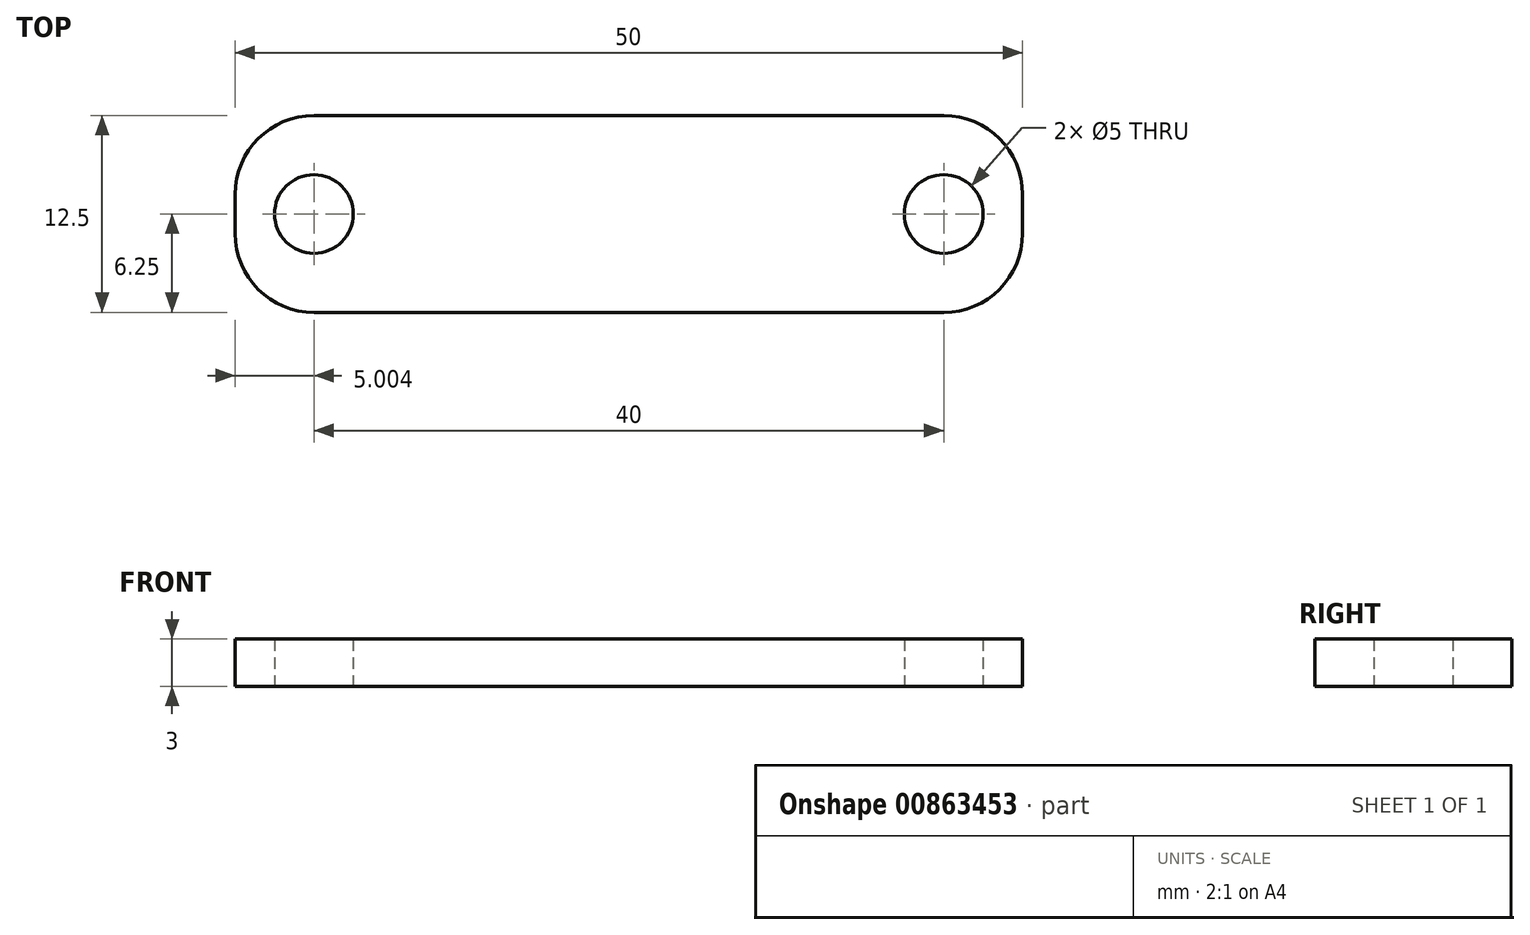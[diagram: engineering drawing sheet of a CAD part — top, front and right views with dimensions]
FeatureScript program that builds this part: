
annotation { "Feature Type Name" : "Feature", "Feature Type Description" : "" }
export const myFeature = defineFeature(function(context is Context, id is Id, definition is map)
    precondition{}
    {
        {
            var Q0;
            Q0=qCreatedBy(makeId("Top.planeOp"),FACE);
            var sketch = newSketch(context, id + "F0", { "sketchPlane" : qUnion([Q0])});
            skLineSegment(sketch, "E0.bottom", {"start": v(23.44, -6.25) * mm, "end": v(-26.56, -6.25) * mm});
            skLineSegment(sketch, "E0.top", {"start": v(23.44, 6.25) * mm, "end": v(-26.56, 6.25) * mm});
            skLineSegment(sketch, "E0.left", {"start": v(23.44, -6.25) * mm, "end": v(23.44, 6.25) * mm});
            skLineSegment(sketch, "E0.right", {"start": v(-26.56, -6.25) * mm, "end": v(-26.56, 6.25) * mm});
            skPoint(sketch, "E0.middle", {"position": v(-1.56, 0) * mm});
            skCircle(sketch, "E1", {"center": v(-21.56, 0) * mm, "radius": 2.5 * mm});
            skPoint(sketch, "E1.centerSnap0", {"position": v(-26.56, 0) * mm});
            skCircle(sketch, "E2", {"center": v(18.44, 0) * mm, "radius": 2.5 * mm});
            skSolve(sketch);
        }
        {
            var Q0;
            Q0=makeQuery(id+"F0.imprint","IMPRINT",FACE,{"disambiguationData":[TD([[makeQuery(id+"F0.imprint","IMPRINT",EDGE,{"derivedFrom":sQuery(id+"F0.wireOp",EDGE,"E0.bottom")}),-1.0]])]});
            extrude(context, id + "F1", {"entities" : qUnion([Q0]), "depth" : 3 * mm, "offsetDistance" : 25 * mm});
        }
        {
            var Q0;
            Q0=makeQuery(id+"F1.opExtrude","SWEPT_EDGE",EDGE,{"disambiguationData":[OSD([sQuery(id+"F0.wireOp",EDGE,"E0.bottom"),sQuery(id+"F0.wireOp",EDGE,"E0.left")])]});
            var Q1;
            Q1=makeQuery(id+"F1.opExtrude","SWEPT_EDGE",EDGE,{"disambiguationData":[OSD([sQuery(id+"F0.wireOp",EDGE,"E0.top"),sQuery(id+"F0.wireOp",EDGE,"E0.left")])]});
            var Q2;
            Q2=makeQuery(id+"F1.opExtrude","SWEPT_EDGE",EDGE,{"disambiguationData":[OSD([sQuery(id+"F0.wireOp",EDGE,"E0.top"),sQuery(id+"F0.wireOp",EDGE,"E0.right")])]});
            var Q3;
            Q3=makeQuery(id+"F1.opExtrude","SWEPT_EDGE",EDGE,{"disambiguationData":[OSD([sQuery(id+"F0.wireOp",EDGE,"E0.bottom"),sQuery(id+"F0.wireOp",EDGE,"E0.right")])]});
            fillet(context, id + "F2", {"entities" : qUnion([Q0, Q1, Q2, Q3]), "radius" : 5 * mm, "tangentPropagation" : true, "allowEdgeOverflow" : false});
        }
    });
